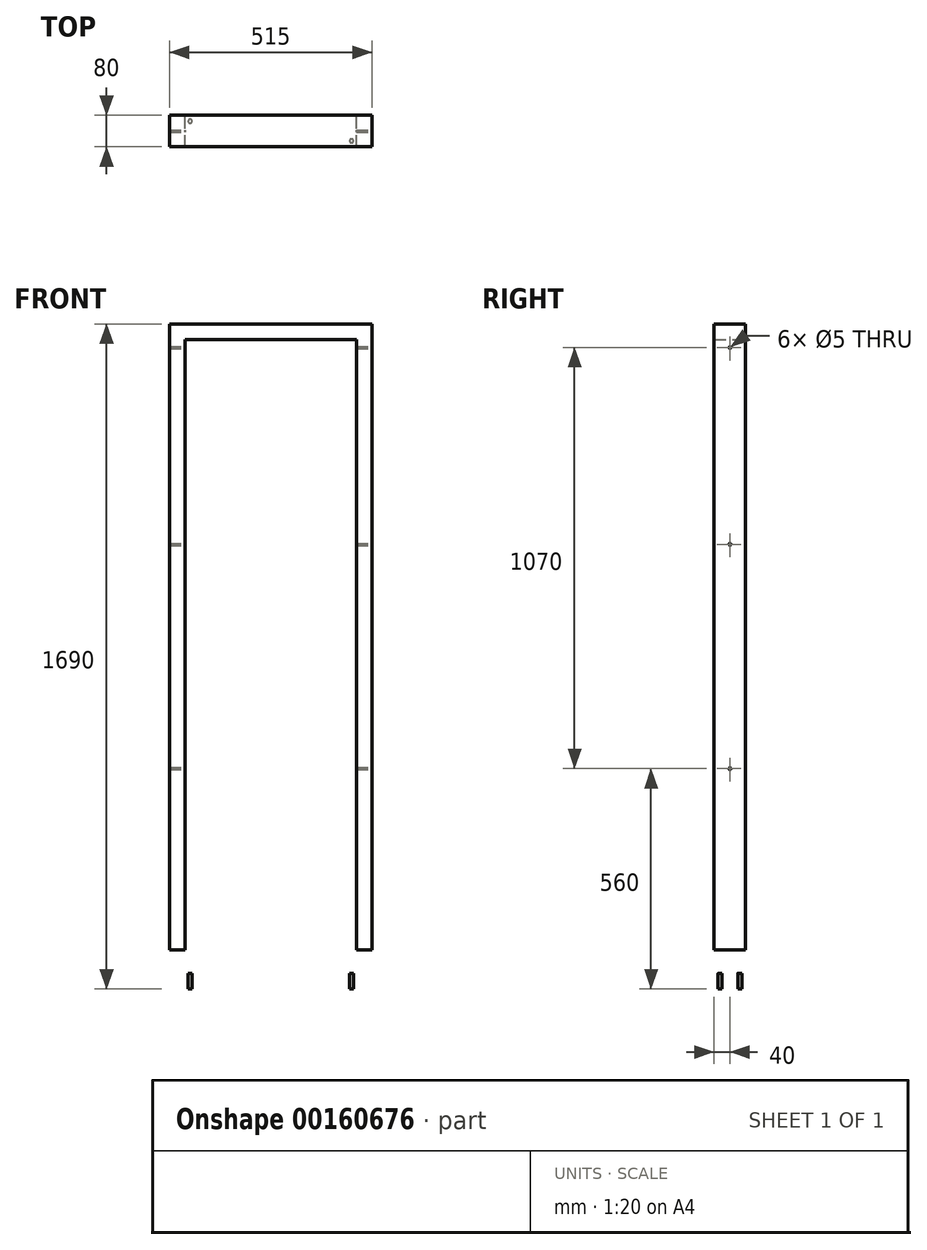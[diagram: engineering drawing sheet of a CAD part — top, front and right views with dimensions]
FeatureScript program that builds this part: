
annotation { "Feature Type Name" : "Feature", "Feature Type Description" : "" }
export const myFeature = defineFeature(function(context is Context, id is Id, definition is map)
    precondition{}
    {
        {
            var Q0;
            Q0=qCreatedBy(makeId("Front.planeOp"),FACE);
            var sketch = newSketch(context, id + "F0", { "sketchPlane" : qUnion([Q0])});
            skLineSegment(sketch, "E0.bottom", {"start": v(-257.5, 845) * mm, "end": v(257.5, 845) * mm});
            skLineSegment(sketch, "E0.top", {"start": v(-257.5, -845) * mm, "end": v(257.5, -845) * mm});
            skLineSegment(sketch, "E0.left", {"start": v(-257.5, 845) * mm, "end": v(-257.5, -845) * mm});
            skLineSegment(sketch, "E0.right", {"start": v(257.5, 845) * mm, "end": v(257.5, -845) * mm});
            skLineSegment(sketch, "E1.0", {"start": v(-217.5, 805) * mm, "end": v(217.5, 805) * mm});
            skLineSegment(sketch, "E1.1", {"start": v(-217.5, 805) * mm, "end": v(-217.5, -805) * mm});
            skLineSegment(sketch, "E1.2", {"start": v(-217.5, -805) * mm, "end": v(217.5, -805) * mm});
            skLineSegment(sketch, "E1.3", {"start": v(217.5, 805) * mm, "end": v(217.5, -805) * mm});
            skSolve(sketch);
        }
        {
            var Q0;
            Q0=makeQuery(id+"F0.imprint","IMPRINT",FACE,{"disambiguationData":[TD([[makeQuery(id+"F0.imprint","IMPRINT",EDGE,{"derivedFrom":sQuery(id+"F0.wireOp",EDGE,"E0.bottom")}),-1.0]])]});
            extrude(context, id + "F1", {"entities" : qUnion([Q0]), "depth" : 80 * mm});
        }
        {
            var Q0;
            Q0=makeQuery(id+"F1.opExtrude","SWEPT_FACE",FACE,{"disambiguationData":[OSD([sQuery(id+"F0.wireOp",EDGE,"E0.top")])]});
            var sketch = newSketch(context, id + "F2", { "sketchPlane" : qUnion([Q0])});
            skCircle(sketch, "E2", {"center": v(-205, 65) * mm, "radius": 5 * mm});
            skLineSegment(sketch, "E3", {"start": v(-257.5, 40) * mm, "end": v(257.5, 40) * mm, "construction": true});
            skCircle(sketch, "E4.MirrorC", {"center": v(-205, 15) * mm, "radius": 5 * mm});
            skCircle(sketch, "E5.MirrorC", {"center": v(205, 65) * mm, "radius": 5 * mm});
            skCircle(sketch, "E6.MirrorC", {"center": v(205, 15) * mm, "radius": 5 * mm});
            skSolve(sketch);
        }
        {
            var Q0;
            Q0=makeQuery(id+"F2.imprint","IMPRINT",FACE,{"disambiguationData":[TD([[makeQuery(id+"F2.imprint","IMPRINT",EDGE,{"derivedFrom":sQuery(id+"F2.wireOp",EDGE,"E2")}),1.0]])]});
            var Q1;
            Q1=makeQuery(id+"F2.imprint","IMPRINT",FACE,{"disambiguationData":[TD([[makeQuery(id+"F2.imprint","IMPRINT",EDGE,{"derivedFrom":sQuery(id+"F2.wireOp",EDGE,"E4.MirrorC")}),-1.0]])]});
            var Q2;
            Q2=makeQuery(id+"F2.imprint","IMPRINT",FACE,{"disambiguationData":[TD([[makeQuery(id+"F2.imprint","IMPRINT",EDGE,{"derivedFrom":sQuery(id+"F2.wireOp",EDGE,"E5.MirrorC")}),-1.0]])]});
            var Q3;
            Q3=makeQuery(id+"F2.imprint","IMPRINT",FACE,{"disambiguationData":[TD([[makeQuery(id+"F2.imprint","IMPRINT",EDGE,{"derivedFrom":sQuery(id+"F2.wireOp",EDGE,"E6.MirrorC")}),1.0]])]});
            extrude(context, id + "F3", {"entities" : qUnion([Q0, Q1, Q2, Q3]), "operationType" : NewBodyOperationType.REMOVE, "oppositeDirection" : true, "depth" : 100 * mm});
        }
        {
            var Q0;
            Q0=qCreatedBy(makeId("Right.planeOp"),FACE);
            var sketch = newSketch(context, id + "F4", { "sketchPlane" : qUnion([Q0])});
            skCircle(sketch, "E7", {"center": v(-40, 285) * mm, "radius": 2.5 * mm});
            skCircle(sketch, "E8", {"center": v(-40, 785) * mm, "radius": 2.5 * mm});
            skCircle(sketch, "E9.MirrorC", {"center": v(-40, -285) * mm, "radius": 2.5 * mm});
            skCircle(sketch, "E10.MirrorC", {"center": v(-40, -785) * mm, "radius": 2.5 * mm});
            skSolve(sketch);
        }
        {
            var Q0;
            Q0 = qSketchRegion(id + "F4", true);
            extrude(context, id + "F5", {"entities" : qUnion([Q0]), "operationType" : NewBodyOperationType.REMOVE, "endBound" : BoundingType.SYMMETRIC, "oppositeDirection" : true, "depth" : 2000 * mm});
        }
    });
